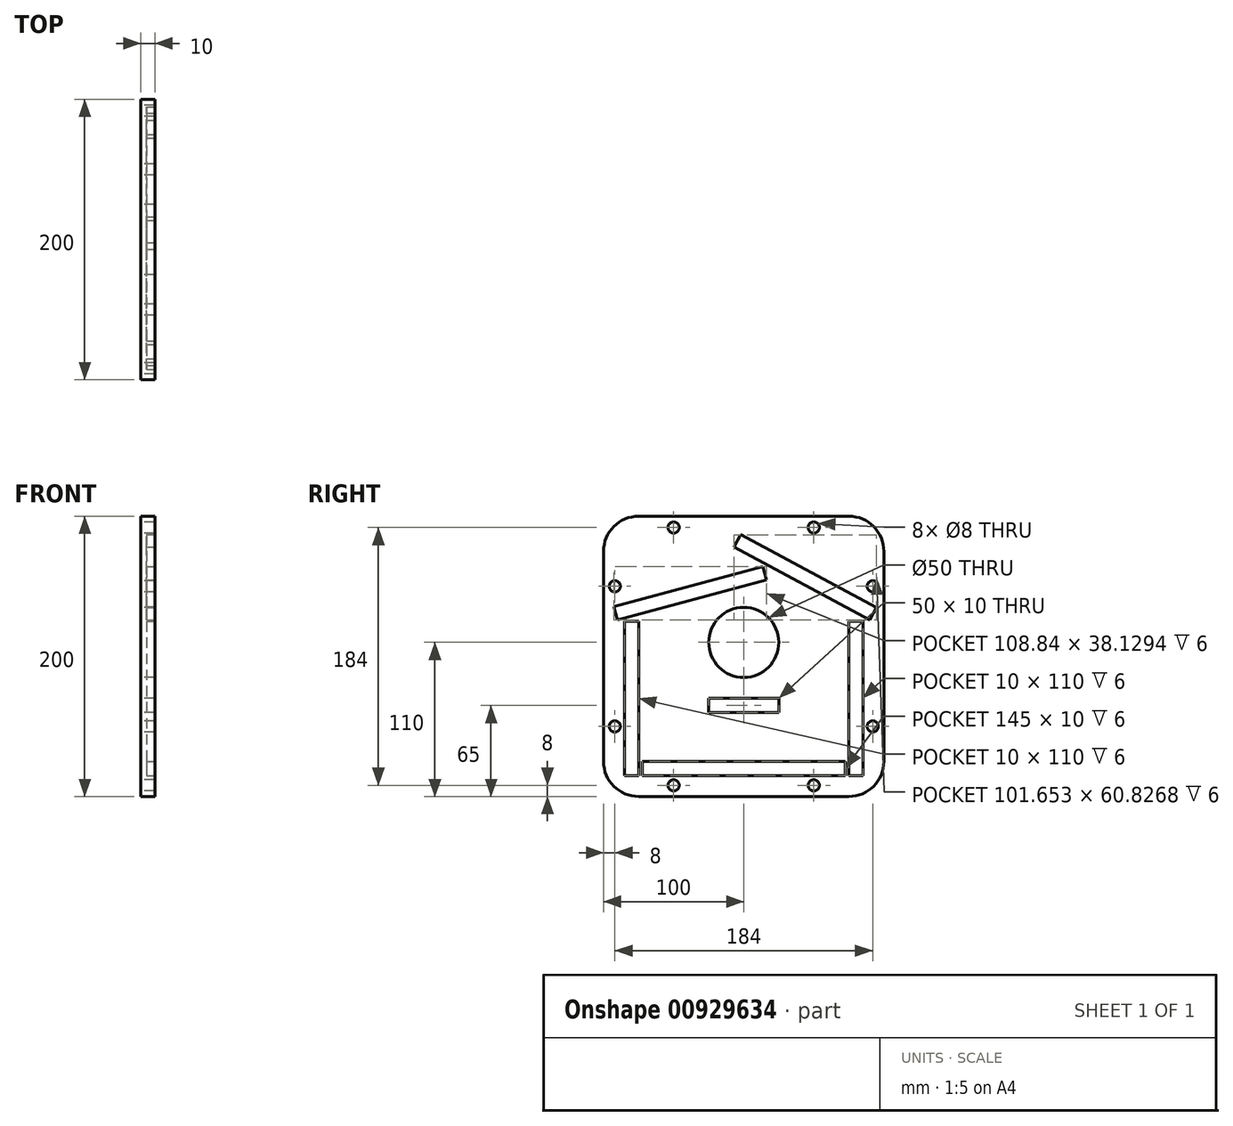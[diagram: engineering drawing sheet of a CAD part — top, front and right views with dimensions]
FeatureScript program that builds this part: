
annotation { "Feature Type Name" : "Feature", "Feature Type Description" : "" }
export const myFeature = defineFeature(function(context is Context, id is Id, definition is map)
    precondition{}
    {
        {
            var Q0;
            Q0=qCreatedBy(makeId("Right.planeOp"),FACE);
            var sketch = newSketch(context, id + "F0", { "sketchPlane" : qUnion([Q0])});
            skLineSegment(sketch, "E0.bottom", {"start": v(0, 0) * mm, "end": v(200, 0) * mm});
            skLineSegment(sketch, "E0.top", {"start": v(0, 200) * mm, "end": v(200, 200) * mm});
            skLineSegment(sketch, "E0.left", {"start": v(0, 0) * mm, "end": v(0, 200) * mm});
            skLineSegment(sketch, "E0.right", {"start": v(200, 0) * mm, "end": v(200, 200) * mm});
            skSolve(sketch);
        }
        {
            var Q0;
            Q0=makeQuery(id+"F0.imprint","IMPRINT",FACE,{"disambiguationData":[TD([[makeQuery(id+"F0.imprint","IMPRINT",EDGE,{"derivedFrom":sQuery(id+"F0.wireOp",EDGE,"E0.bottom")}),1.0]])]});
            extrude(context, id + "F1", {"entities" : qUnion([Q0]), "depth" : 10 * mm, "offsetDistance" : 25.4 * mm});
        }
        {
            var Q0;
            Q0=makeQuery(id+"F1.opExtrude","CAP_FACE",FACE,{"disambiguationData":[OSD([sQuery(id+"F0.wireOp",EDGE,"E0.bottom"),sQuery(id+"F0.wireOp",EDGE,"E0.top"),sQuery(id+"F0.wireOp",EDGE,"E0.left"),sQuery(id+"F0.wireOp",EDGE,"E0.right")])],"isStart":false});
            var sketch = newSketch(context, id + "F2", { "sketchPlane" : qUnion([Q0])});
            skLineSegment(sketch, "E1.bottom", {"start": v(27.5, 25) * mm, "end": v(172.5, 25) * mm});
            skLineSegment(sketch, "E1.top", {"start": v(27.5, 15) * mm, "end": v(172.5, 15) * mm});
            skLineSegment(sketch, "E1.left", {"start": v(27.5, 25) * mm, "end": v(27.5, 15) * mm});
            skLineSegment(sketch, "E1.right", {"start": v(172.5, 25) * mm, "end": v(172.5, 15) * mm});
            skLineSegment(sketch, "E2.bottom", {"start": v(25, 125) * mm, "end": v(15, 125) * mm});
            skLineSegment(sketch, "E2.top", {"start": v(25, 15) * mm, "end": v(15, 15) * mm});
            skLineSegment(sketch, "E2.left", {"start": v(25, 125) * mm, "end": v(25, 15) * mm});
            skLineSegment(sketch, "E2.right", {"start": v(15, 125) * mm, "end": v(15, 15) * mm});
            skLineSegment(sketch, "E3.bottom", {"start": v(175, 125) * mm, "end": v(185, 125) * mm});
            skLineSegment(sketch, "E3.top", {"start": v(175, 15) * mm, "end": v(185, 15) * mm});
            skLineSegment(sketch, "E3.left", {"start": v(175, 125) * mm, "end": v(175, 15) * mm});
            skLineSegment(sketch, "E3.right", {"start": v(185, 125) * mm, "end": v(185, 15) * mm});
            skLineSegment(sketch, "E4", {"start": v(7.41, 135.66) * mm, "end": v(113.66, 164.13) * mm});
            skLineSegment(sketch, "E5", {"start": v(113.66, 164.13) * mm, "end": v(116.25, 154.47) * mm});
            skLineSegment(sketch, "E6", {"start": v(116.25, 154.47) * mm, "end": v(10, 126) * mm});
            skLineSegment(sketch, "E7", {"start": v(10, 126) * mm, "end": v(7.41, 135.66) * mm});
            skLineSegment(sketch, "E8", {"start": v(93.08, 178.02) * mm, "end": v(97.8, 186.83) * mm});
            skLineSegment(sketch, "E9", {"start": v(97.8, 186.83) * mm, "end": v(194.73, 134.81) * mm});
            skLineSegment(sketch, "E10", {"start": v(194.73, 134.81) * mm, "end": v(190, 126) * mm});
            skLineSegment(sketch, "E11", {"start": v(190, 126) * mm, "end": v(93.08, 178.02) * mm});
            skSolve(sketch);
        }
        {
            var Q0;
            Q0=makeQuery(id+"F2.imprint","IMPRINT",FACE,{"disambiguationData":[TD([[makeQuery(id+"F2.imprint","IMPRINT",EDGE,{"derivedFrom":sQuery(id+"F2.wireOp",EDGE,"E4")}),-1.0]])]});
            var Q1;
            Q1=makeQuery(id+"F2.imprint","IMPRINT",FACE,{"disambiguationData":[TD([[makeQuery(id+"F2.imprint","IMPRINT",EDGE,{"derivedFrom":sQuery(id+"F2.wireOp",EDGE,"E8")}),-1.0]])]});
            var Q2;
            Q2=makeQuery(id+"F2.imprint","IMPRINT",FACE,{"disambiguationData":[TD([[makeQuery(id+"F2.imprint","IMPRINT",EDGE,{"derivedFrom":sQuery(id+"F2.wireOp",EDGE,"E2.bottom")}),1.0]])]});
            var Q3;
            Q3=makeQuery(id+"F2.imprint","IMPRINT",FACE,{"disambiguationData":[TD([[makeQuery(id+"F2.imprint","IMPRINT",EDGE,{"derivedFrom":sQuery(id+"F2.wireOp",EDGE,"E1.bottom")}),-1.0]])]});
            var Q4;
            Q4=makeQuery(id+"F2.imprint","IMPRINT",FACE,{"disambiguationData":[TD([[makeQuery(id+"F2.imprint","IMPRINT",EDGE,{"derivedFrom":sQuery(id+"F2.wireOp",EDGE,"E3.bottom")}),-1.0]])]});
            extrude(context, id + "F3", {"entities" : qUnion([Q0, Q1, Q2, Q3, Q4]), "operationType" : NewBodyOperationType.REMOVE, "oppositeDirection" : true, "depth" : 6 * mm, "offsetDistance" : 25 * mm});
        }
        {
            var Q0;
            Q0=makeQuery(id+"F1.opExtrude","CAP_FACE",FACE,{"disambiguationData":[OSD([sQuery(id+"F0.wireOp",EDGE,"E0.bottom"),sQuery(id+"F0.wireOp",EDGE,"E0.top"),sQuery(id+"F0.wireOp",EDGE,"E0.left"),sQuery(id+"F0.wireOp",EDGE,"E0.right")])],"isStart":false});
            var sketch = newSketch(context, id + "F4", { "sketchPlane" : qUnion([Q0])});
            skLineSegment(sketch, "E12.bottom", {"start": v(27.5, 25) * mm, "end": v(172.5, 25) * mm});
            skLineSegment(sketch, "E12.top", {"start": v(27.5, 15) * mm, "end": v(172.5, 15) * mm});
            skLineSegment(sketch, "E12.left", {"start": v(27.5, 25) * mm, "end": v(27.5, 15) * mm});
            skLineSegment(sketch, "E12.right", {"start": v(172.5, 25) * mm, "end": v(172.5, 15) * mm});
            skLineSegment(sketch, "E13.bottom", {"start": v(175, 120) * mm, "end": v(185, 120) * mm});
            skLineSegment(sketch, "E13.top", {"start": v(175, 15) * mm, "end": v(185, 15) * mm});
            skLineSegment(sketch, "E13.left", {"start": v(175, 120) * mm, "end": v(175, 15) * mm});
            skLineSegment(sketch, "E13.right", {"start": v(185, 120) * mm, "end": v(185, 15) * mm});
            skLineSegment(sketch, "E14.bottom", {"start": v(25, 120) * mm, "end": v(15, 120) * mm});
            skLineSegment(sketch, "E14.top", {"start": v(25, 15) * mm, "end": v(15, 15) * mm});
            skLineSegment(sketch, "E14.left", {"start": v(25, 120) * mm, "end": v(25, 15) * mm});
            skLineSegment(sketch, "E14.right", {"start": v(15, 120) * mm, "end": v(15, 15) * mm});
            skLineSegment(sketch, "E15.bottom", {"start": v(75, 190) * mm, "end": v(125, 190) * mm});
            skLineSegment(sketch, "E15.top", {"start": v(75, 180) * mm, "end": v(125, 180) * mm});
            skLineSegment(sketch, "E15.left", {"start": v(75, 190) * mm, "end": v(75, 180) * mm});
            skLineSegment(sketch, "E15.right", {"start": v(125, 190) * mm, "end": v(125, 180) * mm});
            skLineSegment(sketch, "E16", {"start": v(5, 128.78) * mm, "end": v(94.2, 177.5) * mm});
            skLineSegment(sketch, "E17", {"start": v(94.2, 177.5) * mm, "end": v(99, 168.72) * mm});
            skLineSegment(sketch, "E18", {"start": v(5, 128.78) * mm, "end": v(9.78, 120) * mm});
            skLineSegment(sketch, "E19", {"start": v(9.78, 120) * mm, "end": v(99, 168.72) * mm});
            skLineSegment(sketch, "E20", {"start": v(101, 168.72) * mm, "end": v(105.8, 177.5) * mm});
            skLineSegment(sketch, "E21", {"start": v(105.8, 177.5) * mm, "end": v(195, 128.78) * mm});
            skLineSegment(sketch, "E22", {"start": v(195, 128.78) * mm, "end": v(190.22, 120) * mm});
            skLineSegment(sketch, "E23", {"start": v(190.22, 120) * mm, "end": v(101, 168.72) * mm});
            skSolve(sketch);
        }
        {
            var Q0;
            Q0=makeQuery(id+"F1.opExtrude","CAP_FACE",FACE,{"disambiguationData":[OSD([sQuery(id+"F0.wireOp",EDGE,"E0.bottom"),sQuery(id+"F0.wireOp",EDGE,"E0.top"),sQuery(id+"F0.wireOp",EDGE,"E0.left"),sQuery(id+"F0.wireOp",EDGE,"E0.right")])],"isStart":true});
            var sketch = newSketch(context, id + "F5", { "sketchPlane" : qUnion([Q0])});
            skPoint(sketch, "E24", {"position": v(-100, 110) * mm});
            skSolve(sketch);
        }
        {
            var Q0;
            Q0=sQuery(id+"F5.wireOp",VERTEX,"E24");
            var Q1;
            Q1=makeQuery(id+"F1.opExtrude","SWEPT_BODY",BODY,{"disambiguationData":[OSD([sQuery(id+"F0.wireOp",EDGE,"E0.bottom"),sQuery(id+"F0.wireOp",EDGE,"E0.top"),sQuery(id+"F0.wireOp",EDGE,"E0.left"),sQuery(id+"F0.wireOp",EDGE,"E0.right")])]});
            hole(context, id + "F6", {"style" : HoleStyle.SIMPLE, "endStyle" : HoleEndStyle.THROUGH, "holeDiameter" : 50 * mm, "majorDiameter" : 5 * mm, "isTappedThrough" : true, "tappedDepth" : 12 * mm, "tapClearance" : 3, "locations" : qUnion([Q0]), "scope" : qUnion([Q1])});
        }
        {
            var Q0;
            Q0=makeQuery(id+"F1.opExtrude","CAP_FACE",FACE,{"disambiguationData":[OSD([sQuery(id+"F0.wireOp",EDGE,"E0.bottom"),sQuery(id+"F0.wireOp",EDGE,"E0.top"),sQuery(id+"F0.wireOp",EDGE,"E0.left"),sQuery(id+"F0.wireOp",EDGE,"E0.right")])],"isStart":true});
            var sketch = newSketch(context, id + "F7", { "sketchPlane" : qUnion([Q0])});
            skLineSegment(sketch, "E25.bottom", {"start": v(-125, 70) * mm, "end": v(-75, 70) * mm});
            skLineSegment(sketch, "E25.top", {"start": v(-125, 60) * mm, "end": v(-75, 60) * mm});
            skLineSegment(sketch, "E25.left", {"start": v(-125, 70) * mm, "end": v(-125, 60) * mm});
            skLineSegment(sketch, "E25.right", {"start": v(-75, 70) * mm, "end": v(-75, 60) * mm});
            skSolve(sketch);
        }
        {
            var Q0;
            Q0=makeQuery(id+"F7.imprint","IMPRINT",FACE,{"disambiguationData":[TD([[makeQuery(id+"F7.imprint","IMPRINT",EDGE,{"derivedFrom":sQuery(id+"F7.wireOp",EDGE,"E25.bottom")}),-1.0]])]});
            extrude(context, id + "F8", {"entities" : qUnion([Q0]), "operationType" : NewBodyOperationType.REMOVE, "endBound" : BoundingType.UP_TO_NEXT, "oppositeDirection" : true, "depth" : 25 * mm, "offsetDistance" : 25 * mm});
        }
        {
            var Q0;
            Q0=makeQuery(id+"F1.opExtrude","CAP_FACE",FACE,{"disambiguationData":[OSD([sQuery(id+"F0.wireOp",EDGE,"E0.bottom"),sQuery(id+"F0.wireOp",EDGE,"E0.top"),sQuery(id+"F0.wireOp",EDGE,"E0.left"),sQuery(id+"F0.wireOp",EDGE,"E0.right")])],"isStart":true});
            var sketch = newSketch(context, id + "F9", { "sketchPlane" : qUnion([Q0])});
            skPoint(sketch, "E26", {"position": v(-150, 192) * mm});
            skPoint(sketch, "E27", {"position": v(-50, 192) * mm});
            skPoint(sketch, "E28", {"position": v(-8, 150) * mm});
            skPoint(sketch, "E29", {"position": v(-8, 50) * mm});
            skPoint(sketch, "E30", {"position": v(-50, 8) * mm});
            skPoint(sketch, "E31", {"position": v(-150, 8) * mm});
            skPoint(sketch, "E32", {"position": v(-192, 50) * mm});
            skPoint(sketch, "E33", {"position": v(-192, 150) * mm});
            skSolve(sketch);
        }
        {
            var Q0;
            Q0=sQuery(id+"F9.wireOp",VERTEX,"E26");
            var Q1;
            Q1=sQuery(id+"F9.wireOp",VERTEX,"E33");
            var Q2;
            Q2=sQuery(id+"F9.wireOp",VERTEX,"E27");
            var Q3;
            Q3=sQuery(id+"F9.wireOp",VERTEX,"E28");
            var Q4;
            Q4=sQuery(id+"F9.wireOp",VERTEX,"E30");
            var Q5;
            Q5=sQuery(id+"F9.wireOp",VERTEX,"E29");
            var Q6;
            Q6=sQuery(id+"F9.wireOp",VERTEX,"E31");
            var Q7;
            Q7=sQuery(id+"F9.wireOp",VERTEX,"E32");
            var Q8;
            Q8=makeQuery(id+"F1.opExtrude","SWEPT_BODY",BODY,{"disambiguationData":[OSD([sQuery(id+"F0.wireOp",EDGE,"E0.bottom"),sQuery(id+"F0.wireOp",EDGE,"E0.top"),sQuery(id+"F0.wireOp",EDGE,"E0.left"),sQuery(id+"F0.wireOp",EDGE,"E0.right")])]});
            hole(context, id + "F10", {"style" : HoleStyle.SIMPLE, "endStyle" : HoleEndStyle.THROUGH, "holeDiameter" : 8 * mm, "majorDiameter" : 6.35 * mm, "isTappedThrough" : true, "tappedDepth" : 12.7 * mm, "tapClearance" : 3, "locations" : qUnion([Q0, Q1, Q2, Q3, Q4, Q5, Q6, Q7]), "scope" : qUnion([Q8])});
        }
        {
            var Q0;
            Q0=makeQuery(id+"F1.opExtrude","SWEPT_EDGE",EDGE,{"disambiguationData":[OSD([sQuery(id+"F0.wireOp",EDGE,"E0.top"),sQuery(id+"F0.wireOp",EDGE,"E0.left")])]});
            var Q1;
            Q1=makeQuery(id+"F1.opExtrude","SWEPT_EDGE",EDGE,{"disambiguationData":[OSD([sQuery(id+"F0.wireOp",EDGE,"E0.bottom"),sQuery(id+"F0.wireOp",EDGE,"E0.left")])]});
            var Q2;
            Q2=makeQuery(id+"F1.opExtrude","SWEPT_EDGE",EDGE,{"disambiguationData":[OSD([sQuery(id+"F0.wireOp",EDGE,"E0.top"),sQuery(id+"F0.wireOp",EDGE,"E0.right")])]});
            var Q3;
            Q3=makeQuery(id+"F1.opExtrude","SWEPT_EDGE",EDGE,{"disambiguationData":[OSD([sQuery(id+"F0.wireOp",EDGE,"E0.bottom"),sQuery(id+"F0.wireOp",EDGE,"E0.right")])]});
            fillet(context, id + "F11", {"entities" : qUnion([Q0, Q1, Q2, Q3]), "radius" : 25 * mm, "tangentPropagation" : true, "allowEdgeOverflow" : false});
        }
    });
